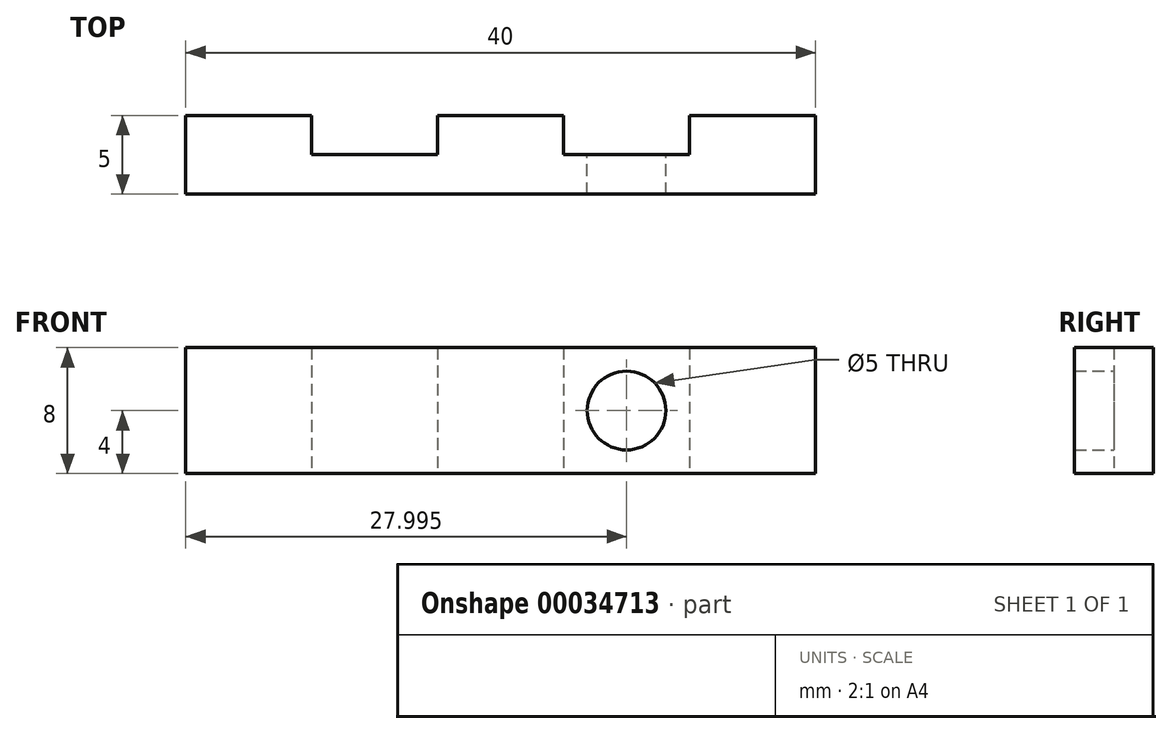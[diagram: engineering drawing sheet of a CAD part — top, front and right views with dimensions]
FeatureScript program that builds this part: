
annotation { "Feature Type Name" : "Feature", "Feature Type Description" : "" }
export const myFeature = defineFeature(function(context is Context, id is Id, definition is map)
    precondition{}
    {
        {
            var Q0;
            Q0=qCreatedBy(makeId("Top.planeOp"),FACE);
            var sketch = newSketch(context, id + "F0", { "sketchPlane" : qUnion([Q0])});
            skLineSegment(sketch, "E0.bottom", {"start": v(-7.98, 0) * mm, "end": v(0.02, 0) * mm});
            skLineSegment(sketch, "E0.top", {"start": v(-7.98, 5) * mm, "end": v(0.02, 5) * mm});
            skLineSegment(sketch, "E0.left", {"start": v(-7.98, 0) * mm, "end": v(-7.98, 5) * mm});
            skLineSegment(sketch, "E0.right", {"start": v(0.02, 0) * mm, "end": v(0.02, 5) * mm});
            skLineSegment(sketch, "E1.bottom", {"start": v(0.02, 2.5) * mm, "end": v(8.02, 2.5) * mm});
            skLineSegment(sketch, "E1.top", {"start": v(0.02, 0) * mm, "end": v(8.02, 0) * mm});
            skLineSegment(sketch, "E1.left", {"start": v(0.02, 2.5) * mm, "end": v(0.02, 0) * mm, "construction": true});
            skLineSegment(sketch, "E1.right", {"start": v(8.02, 2.5) * mm, "end": v(8.02, 0) * mm});
            skLineSegment(sketch, "E2.bottom", {"start": v(8.02, 0) * mm, "end": v(16.02, 0) * mm});
            skLineSegment(sketch, "E2.top", {"start": v(8.02, 5) * mm, "end": v(16.02, 5) * mm});
            skLineSegment(sketch, "E2.left", {"start": v(8.02, 0) * mm, "end": v(8.02, 5) * mm});
            skLineSegment(sketch, "E2.right", {"start": v(16.02, 0) * mm, "end": v(16.02, 5) * mm});
            skLineSegment(sketch, "E3.bottom", {"start": v(16.02, 2.5) * mm, "end": v(24.02, 2.5) * mm});
            skLineSegment(sketch, "E3.top", {"start": v(16.02, 0) * mm, "end": v(24.02, 0) * mm});
            skLineSegment(sketch, "E3.left", {"start": v(16.02, 2.5) * mm, "end": v(16.02, 0) * mm});
            skLineSegment(sketch, "E3.right", {"start": v(24.02, 2.5) * mm, "end": v(24.02, 0) * mm});
            skLineSegment(sketch, "E4.bottom", {"start": v(24.02, 0) * mm, "end": v(32.02, 0) * mm});
            skLineSegment(sketch, "E4.top", {"start": v(24.02, 5) * mm, "end": v(32.02, 5) * mm});
            skLineSegment(sketch, "E4.left", {"start": v(24.02, 0) * mm, "end": v(24.02, 5) * mm});
            skLineSegment(sketch, "E4.right", {"start": v(32.02, 0) * mm, "end": v(32.02, 5) * mm});
            skSolve(sketch);
        }
        {
            var Q0;
            {var subQ1=sQuery(id+"F0.wireOp",EDGE,"E0.bottom");Q0=makeQuery(id+"F0.imprint","IMPRINT",FACE,{"disambiguationData":[TD([[makeQuery(id+"F0.imprint","IMPRINT",EDGE,{"derivedFrom":subQ1}),1.0]])]});}
            var Q1;
            {var subQ2=sQuery(id+"F0.wireOp",EDGE,"E1.bottom");Q1=makeQuery(id+"F0.imprint","IMPRINT",FACE,{"disambiguationData":[TD([[makeQuery(id+"F0.imprint","IMPRINT",EDGE,{"derivedFrom":subQ2}),-1.0]])]});}
            var Q2;
            {var subQ3=sQuery(id+"F0.wireOp",EDGE,"E2.bottom");Q2=makeQuery(id+"F0.imprint","IMPRINT",FACE,{"disambiguationData":[TD([[makeQuery(id+"F0.imprint","IMPRINT",EDGE,{"derivedFrom":subQ3}),1.0]])]});}
            var Q3;
            {var subQ0=sQuery(id+"F0.wireOp",EDGE,"E3.bottom");Q3=makeQuery(id+"F0.imprint","IMPRINT",FACE,{"disambiguationData":[TD([[makeQuery(id+"F0.imprint","IMPRINT",EDGE,{"derivedFrom":subQ0}),-1.0]])]});}
            var Q4;
            {var subQ3=sQuery(id+"F0.wireOp",EDGE,"E4.bottom");Q4=makeQuery(id+"F0.imprint","IMPRINT",FACE,{"disambiguationData":[TD([[makeQuery(id+"F0.imprint","IMPRINT",EDGE,{"derivedFrom":subQ3}),1.0]])]});}
            extrude(context, id + "F1", {"entities" : qUnion([Q0, Q1, Q2, Q3, Q4]), "depth" : 8 * mm});
        }
        {
            var Q0;
            Q0=makeQuery(id+"F1.opExtrude","SWEPT_FACE",FACE,{"disambiguationData":[OSD([sQuery(id+"F0.wireOp",EDGE,"E3.bottom")])]});
            var sketch = newSketch(context, id + "F2", { "sketchPlane" : qUnion([Q0])});
            skLineSegment(sketch, "E5", {"start": v(-20.02, 8) * mm, "end": v(-20.02, 0) * mm, "construction": true});
            skCircle(sketch, "E6", {"center": v(-20.02, 4) * mm, "radius": 2.5 * mm});
            skLineSegment(sketch, "E7", {"start": v(-24.02, 4) * mm, "end": v(-16.02, 4) * mm, "construction": true});
            skLineSegment(sketch, "E8.0.0", {"start": v(-16.02, 0) * mm, "end": v(-8.02, 0) * mm});
            skLineSegment(sketch, "E8.0.1", {"start": v(-8.02, 0) * mm, "end": v(-8.02, 8) * mm});
            skLineSegment(sketch, "E8.0.2", {"start": v(-8.02, 8) * mm, "end": v(-16.02, 8) * mm});
            skLineSegment(sketch, "E8.0.3", {"start": v(-16.02, 8) * mm, "end": v(-16.02, 0) * mm});
            skLineSegment(sketch, "E9", {"start": v(-12.02, 0) * mm, "end": v(-12.02, 8) * mm});
            skCircle(sketch, "E10.MirrorC", {"center": v(-4.02, 4) * mm, "radius": 2.5 * mm});
            skSolve(sketch);
        }
        {
            var Q0;
            Q0=makeQuery(id+"F2.imprint","IMPRINT",FACE,{"disambiguationData":[TD([[makeQuery(id+"F2.imprint","IMPRINT",EDGE,{"derivedFrom":sQuery(id+"F2.wireOp",EDGE,"E6")}),1.0]])]});
            var Q1;
            Q1=makeQuery(id+"F2.imprint","IMPRINT",FACE,{"disambiguationData":[TD([[makeQuery(id+"F2.imprint","IMPRINT",EDGE,{"derivedFrom":sQuery(id+"F2.wireOp",EDGE,"E10.MirrorC")}),-1.0]])]});
            extrude(context, id + "F3", {"entities" : qUnion([Q0, Q1]), "operationType" : NewBodyOperationType.REMOVE, "oppositeDirection" : true, "depth" : 4.06 * mm});
        }
    });
